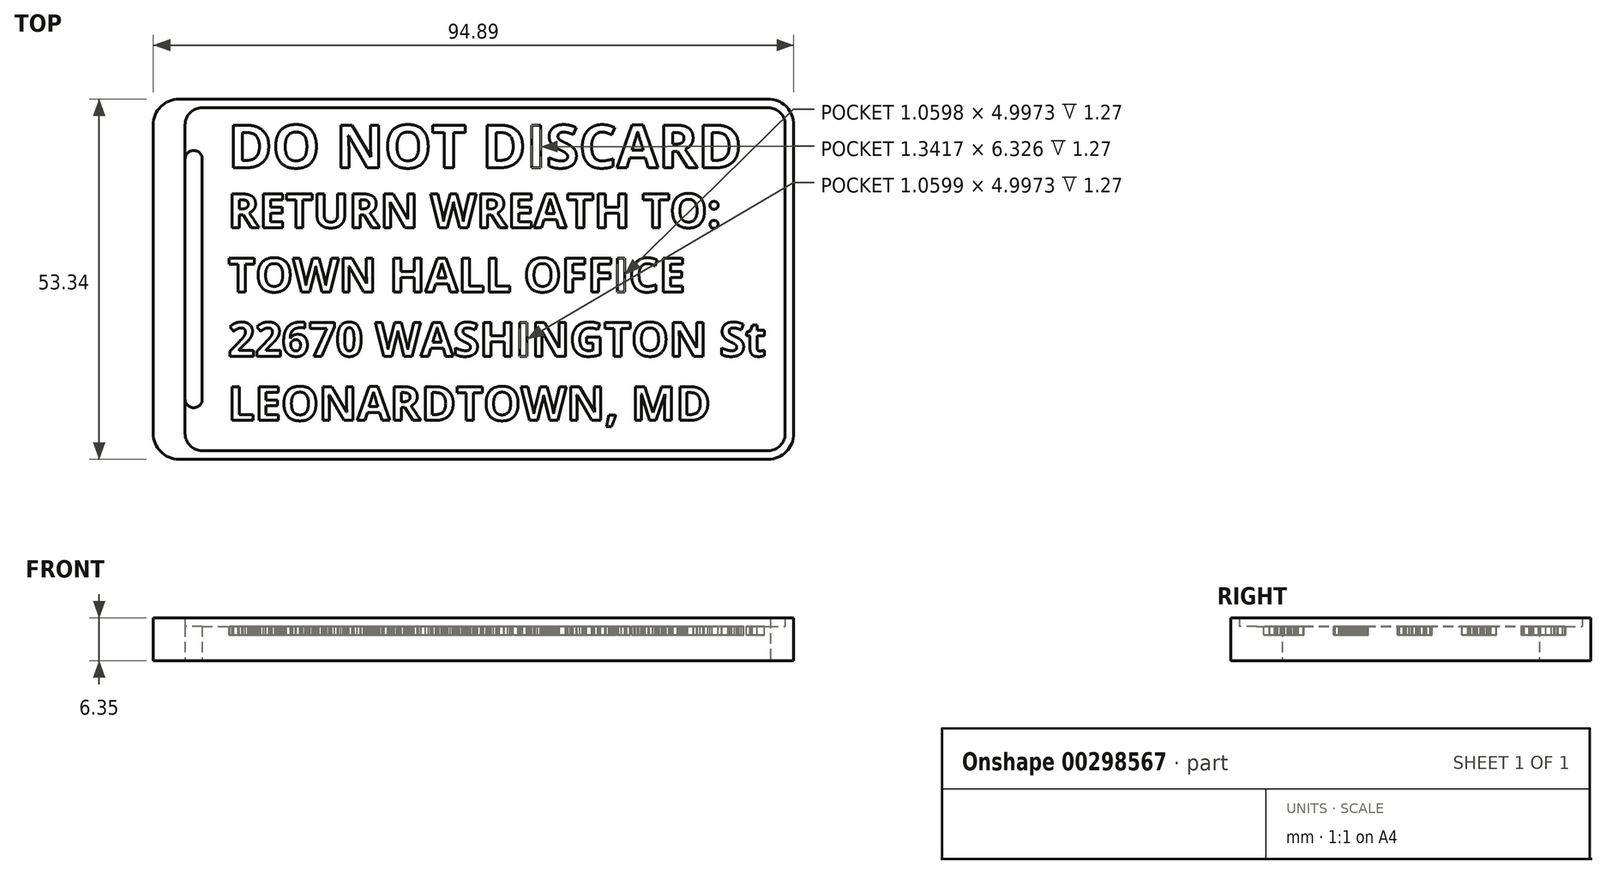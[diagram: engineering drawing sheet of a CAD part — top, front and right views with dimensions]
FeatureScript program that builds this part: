
annotation { "Feature Type Name" : "Feature", "Feature Type Description" : "" }
export const myFeature = defineFeature(function(context is Context, id is Id, definition is map)
    precondition{}
    {
        {
            var Q0;
            Q0=qCreatedBy(makeId("Top.planeOp"),FACE);
            var sketch = newSketch(context, id + "F0", { "sketchPlane" : qUnion([Q0])});
            skLineSegment(sketch, "E0.bottom", {"start": v(2.54, 0) * mm, "end": v(86.36, 0) * mm});
            skLineSegment(sketch, "E0.top", {"start": v(2.54, 50.8) * mm, "end": v(86.36, 50.8) * mm});
            skLineSegment(sketch, "E0.left", {"start": v(0, 2.54) * mm, "end": v(0, 48.26) * mm});
            skLineSegment(sketch, "E0.right", {"start": v(88.9, 2.54) * mm, "end": v(88.9, 48.26) * mm});
            skPoint(sketch, "E1.visualSharp", {"position": v(0, 50.8) * mm});
            skArc(sketch, "E1.filletArc", {"start": v(2.54, 50.8) * mm, "mid": v(0.74, 50.06) * mm, "end": v(0, 48.26) * mm});
            skPoint(sketch, "E2.visualSharp", {"position": v(88.9, 50.8) * mm});
            skArc(sketch, "E2.filletArc", {"start": v(88.9, 48.26) * mm, "mid": v(88.16, 50.06) * mm, "end": v(86.36, 50.8) * mm});
            skPoint(sketch, "E3.visualSharp", {"position": v(88.9, 0) * mm});
            skArc(sketch, "E3.filletArc", {"start": v(86.36, 0) * mm, "mid": v(88.16, 0.74) * mm, "end": v(88.9, 2.54) * mm});
            skPoint(sketch, "E4.visualSharp", {"position": v(0, 0) * mm});
            skArc(sketch, "E4.filletArc", {"start": v(0, 2.54) * mm, "mid": v(0.74, 0.74) * mm, "end": v(2.54, 0) * mm});
            skLineSegment(sketch, "E5.2", {"start": v(2.9, -1.27) * mm, "end": v(86.36, -1.27) * mm});
            skArc(sketch, "E5.4", {"start": v(86.36, -1.27) * mm, "mid": v(89.05, -0.15) * mm, "end": v(90.17, 2.54) * mm});
            skLineSegment(sketch, "E5.5", {"start": v(90.17, 2.54) * mm, "end": v(90.17, 48.26) * mm});
            skArc(sketch, "E5.6", {"start": v(90.17, 48.26) * mm, "mid": v(89.18, 50.84) * mm, "end": v(86.72, 52.07) * mm});
            skLineSegment(sketch, "E5.7", {"start": v(2.9, 52.07) * mm, "end": v(86.72, 52.07) * mm});
            skLineSegment(sketch, "E6", {"start": v(2.9, 52.07) * mm, "end": v(-0.91, 52.07) * mm});
            skLineSegment(sketch, "E7", {"start": v(2.9, -1.27) * mm, "end": v(-0.91, -1.27) * mm});
            skLineSegment(sketch, "E8", {"start": v(-4.72, 2.54) * mm, "end": v(-4.72, 48.26) * mm});
            skPoint(sketch, "E9.visualSharp", {"position": v(-4.72, 52.07) * mm});
            skArc(sketch, "E9.filletArc", {"start": v(-0.91, 52.07) * mm, "mid": v(-3.6, 50.96) * mm, "end": v(-4.72, 48.26) * mm});
            skPoint(sketch, "E10.visualSharp", {"position": v(-4.72, -1.27) * mm});
            skArc(sketch, "E10.filletArc", {"start": v(-4.72, 2.54) * mm, "mid": v(-3.6, -0.15) * mm, "end": v(-0.91, -1.27) * mm});
            skLineSegment(sketch, "E11", {"start": v(0, 25.4) * mm, "end": v(67.57, 25.4) * mm, "construction": true});
            skPoint(sketch, "E11.endSnap0", {"position": v(0, 25.4) * mm});
            skArc(sketch, "E12", {"start": v(2.54, 43.18) * mm, "mid": v(1.27, 44.45) * mm, "end": v(0, 43.18) * mm});
            skPoint(sketch, "E12.first.point", {"position": v(0, 43.18) * mm});
            skPoint(sketch, "E12.second.point", {"position": v(2.54, 43.18) * mm});
            skLineSegment(sketch, "E13", {"start": v(2.54, 43.18) * mm, "end": v(2.54, 25.4) * mm});
            skLineSegment(sketch, "E14.MirrorCS", {"start": v(2.54, 7.62) * mm, "end": v(2.54, 25.4) * mm});
            skArc(sketch, "E15.MirrorCS", {"start": v(2.54, 7.62) * mm, "mid": v(1.27, 6.35) * mm, "end": v(0, 7.62) * mm});
            skSolve(sketch);
        }
        {
            var Q0;
            Q0=makeQuery(id+"F0.imprint","IMPRINT",FACE,{"disambiguationData":[TD([[makeQuery(id+"F0.imprint","IMPRINT",EDGE,{"derivedFrom":sQuery(id+"F0.wireOp",EDGE,"E0.bottom")}),-1.0]])]});
            extrude(context, id + "F1", {"entities" : qUnion([Q0]), "depth" : 6.35 * mm});
        }
        {
            var Q0;
            Q0=makeQuery(id+"F0.imprint","IMPRINT",FACE,{"disambiguationData":[TD([[makeQuery(id+"F0.imprint","IMPRINT",EDGE,{"derivedFrom":sQuery(id+"F0.wireOp",EDGE,"E0.bottom")}),1.0]])]});
            extrude(context, id + "F2", {"entities" : qUnion([Q0]), "operationType" : NewBodyOperationType.ADD, "depth" : 5.08 * mm});
        }
        {
            var Q0;
            Q0=makeQuery(id+"F2.opExtrude","CAP_FACE",FACE,{"disambiguationData":[OSD([sQuery(id+"F0.wireOp",EDGE,"E0.bottom"),sQuery(id+"F0.wireOp",EDGE,"E0.top"),sQuery(id+"F0.wireOp",EDGE,"E0.left"),sQuery(id+"F0.wireOp",EDGE,"E0.right"),sQuery(id+"F0.wireOp",EDGE,"E1.filletArc"),sQuery(id+"F0.wireOp",EDGE,"E2.filletArc"),sQuery(id+"F0.wireOp",EDGE,"E3.filletArc"),sQuery(id+"F0.wireOp",EDGE,"E4.filletArc"),sQuery(id+"F0.wireOp",EDGE,"E12"),sQuery(id+"F0.wireOp",EDGE,"E13"),sQuery(id+"F0.wireOp",EDGE,"E14.MirrorCS"),sQuery(id+"F0.wireOp",EDGE,"E15.MirrorCS")])],"isStart":false});
            var sketch = newSketch(context, id + "F3", { "sketchPlane" : qUnion([Q0])});
            skText(sketch, "E16", { "text": "DO NOT DISCARD", "fontName": "OpenSans-Bold.ttf"});
            skText(sketch, "E17", { "text": "RETURN WREATH TO:\nTOWN HALL OFFICE\n22670 WASHINGTON St\nLEONARDTOWN, MD\n", "fontName": "OpenSans-Bold.ttf"});
            const initialGuessF3  = {"E16": [0.00635, 0.04188, 1, 0, 0.00638], "E17": [0.00635, 0.03303, 1, 0, 0.00504]};
            skSetInitialGuess(sketch, initialGuessF3);
            skSolve(sketch);
        }
        {
            var Q0;
            Q0=qSketchRegion(id+"F3",true);
            extrude(context, id + "F4", {"entities" : qUnion([Q0]), "operationType" : NewBodyOperationType.REMOVE, "oppositeDirection" : true, "depth" : 1.27 * mm});
        }
    });
